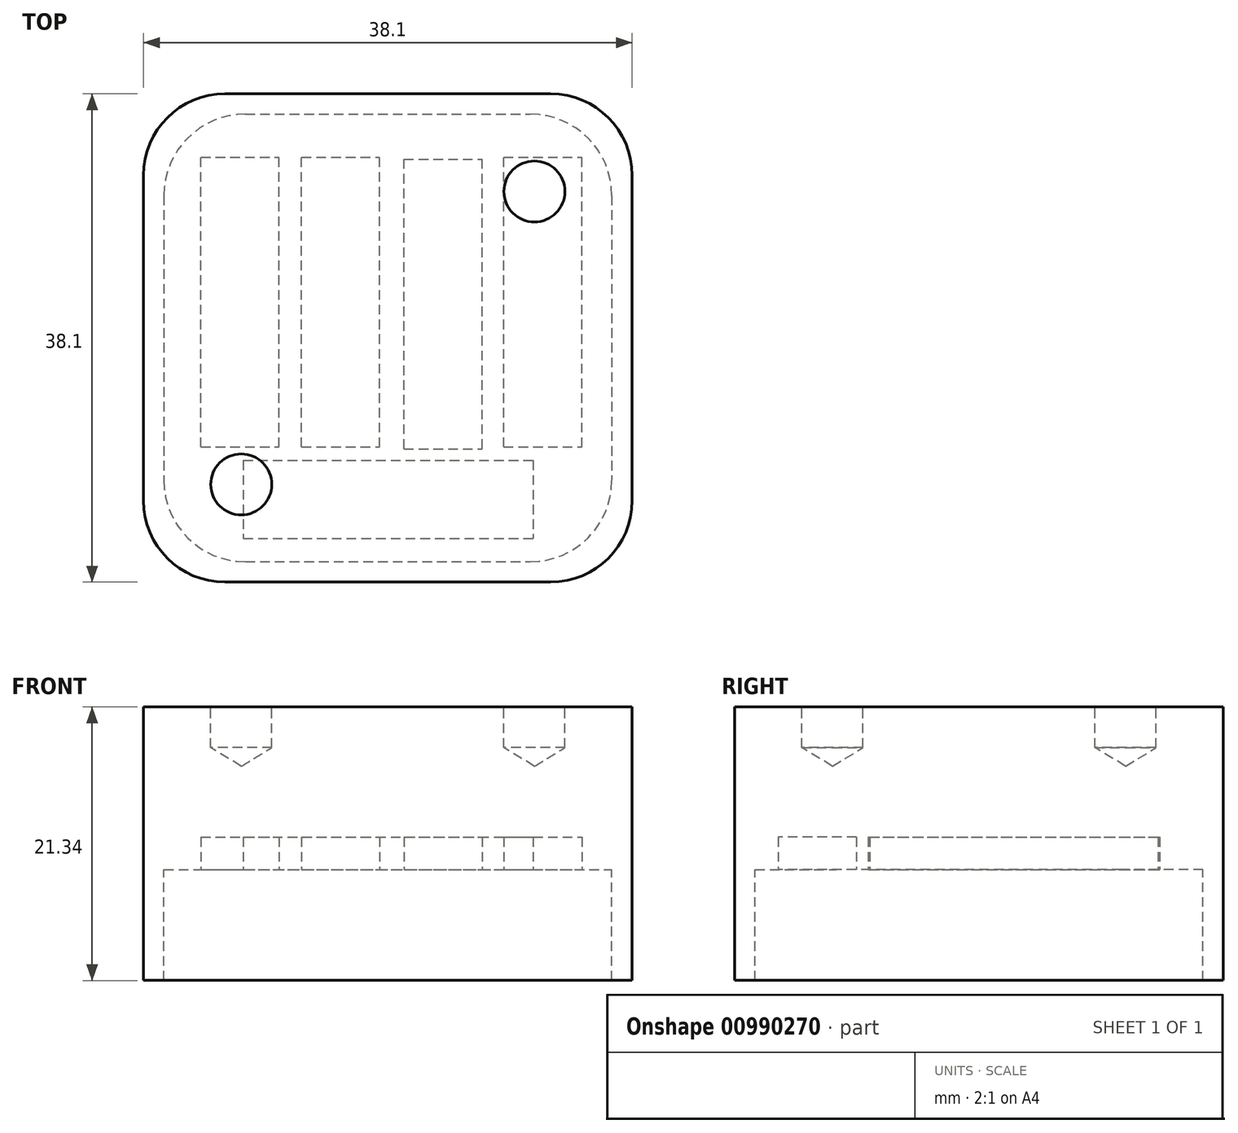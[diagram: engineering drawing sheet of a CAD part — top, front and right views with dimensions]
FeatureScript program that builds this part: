
annotation { "Feature Type Name" : "Feature", "Feature Type Description" : "" }
export const myFeature = defineFeature(function(context is Context, id is Id, definition is map)
    precondition{}
    {
        {
            var Q0;
            Q0=qCreatedBy(makeId("Top.planeOp"),FACE);
            var sketch = newSketch(context, id + "F0", { "sketchPlane" : qUnion([Q0])});
            skLineSegment(sketch, "E0.bottom", {"start": v(15.01, 15.04) * mm, "end": v(40.41, 15.04) * mm});
            skLineSegment(sketch, "E0.top", {"start": v(15.01, -23.06) * mm, "end": v(40.41, -23.06) * mm});
            skLineSegment(sketch, "E0.left", {"start": v(8.66, 8.7) * mm, "end": v(8.66, -16.7) * mm});
            skLineSegment(sketch, "E0.right", {"start": v(46.76, 8.7) * mm, "end": v(46.76, -16.7) * mm});
            skPoint(sketch, "E1.visualSharp", {"position": v(46.76, 15.04) * mm});
            skArc(sketch, "E1.filletArc", {"start": v(46.76, 8.7) * mm, "mid": v(44.9, 13.19) * mm, "end": v(40.41, 15.04) * mm});
            skPoint(sketch, "E2.visualSharp", {"position": v(8.66, 15.04) * mm});
            skArc(sketch, "E2.filletArc", {"start": v(15.01, 15.04) * mm, "mid": v(10.52, 13.19) * mm, "end": v(8.66, 8.7) * mm});
            skPoint(sketch, "E3.visualSharp", {"position": v(8.66, -23.06) * mm});
            skArc(sketch, "E3.filletArc", {"start": v(8.66, -16.7) * mm, "mid": v(10.52, -21.2) * mm, "end": v(15.01, -23.06) * mm});
            skPoint(sketch, "E4.visualSharp", {"position": v(46.76, -23.06) * mm});
            skArc(sketch, "E4.filletArc", {"start": v(40.41, -23.06) * mm, "mid": v(44.9, -21.2) * mm, "end": v(46.76, -16.7) * mm});
            skSolve(sketch);
        }
        {
            var Q0;
            Q0 = qSketchRegion(id + "F0", true);
            extrude(context, id + "F1", {"entities" : qUnion([Q0]), "depth" : 12.7 * mm, "offsetDistance" : 25.4 * mm});
        }
        {
            var Q0;
            Q0=makeQuery(id+"F1.opExtrude","CAP_FACE",FACE,{"disambiguationData":[OSD([sQuery(id+"F0.wireOp",EDGE,"E0.bottom"),sQuery(id+"F0.wireOp",EDGE,"E0.top"),sQuery(id+"F0.wireOp",EDGE,"E0.left"),sQuery(id+"F0.wireOp",EDGE,"E0.right"),sQuery(id+"F0.wireOp",EDGE,"E1.filletArc"),sQuery(id+"F0.wireOp",EDGE,"E2.filletArc"),sQuery(id+"F0.wireOp",EDGE,"E3.filletArc"),sQuery(id+"F0.wireOp",EDGE,"E4.filletArc")])],"isStart":false});
            var sketch = newSketch(context, id + "F2", { "sketchPlane" : qUnion([Q0])});
            skLineSegment(sketch, "E5.0", {"start": v(16.6, 13.46) * mm, "end": v(38.82, 13.46) * mm});
            skLineSegment(sketch, "E5.1", {"start": v(10.25, 7.1) * mm, "end": v(10.25, -15.12) * mm});
            skLineSegment(sketch, "E5.2", {"start": v(16.6, -21.47) * mm, "end": v(38.82, -21.47) * mm});
            skLineSegment(sketch, "E5.3", {"start": v(45.17, 7.1) * mm, "end": v(45.17, -15.12) * mm});
            skPoint(sketch, "E6.visualSharp", {"position": v(10.25, -21.47) * mm});
            skArc(sketch, "E6.filletArc", {"start": v(10.25, -15.12) * mm, "mid": v(12.1, -19.6) * mm, "end": v(16.6, -21.47) * mm});
            skPoint(sketch, "E7.visualSharp", {"position": v(45.17, -21.47) * mm});
            skArc(sketch, "E7.filletArc", {"start": v(38.82, -21.47) * mm, "mid": v(43.31, -19.6) * mm, "end": v(45.17, -15.12) * mm});
            skPoint(sketch, "E8.visualSharp", {"position": v(45.17, 13.46) * mm});
            skArc(sketch, "E8.filletArc", {"start": v(45.17, 7.1) * mm, "mid": v(43.31, 11.6) * mm, "end": v(38.82, 13.46) * mm});
            skPoint(sketch, "E9.visualSharp", {"position": v(10.25, 13.46) * mm});
            skArc(sketch, "E9.filletArc", {"start": v(16.6, 13.46) * mm, "mid": v(12.1, 11.6) * mm, "end": v(10.25, 7.1) * mm});
            skSolve(sketch);
        }
        {
            var Q0;
            Q0=makeQuery(id+"F2.imprint","IMPRINT",FACE,{"disambiguationData":[TD([[makeQuery(id+"F2.imprint","IMPRINT",EDGE,{"derivedFrom":sQuery(id+"F2.wireOp",EDGE,"E5.0")}),1.0]])]});
            extrude(context, id + "F3", {"entities" : qUnion([Q0]), "operationType" : NewBodyOperationType.ADD, "oppositeDirection" : true, "depth" : 21.34 * mm, "offsetDistance" : 25.4 * mm});
        }
        {
            var Q0;
            Q0=makeQuery(id+"F1.opExtrude","CAP_FACE",FACE,{"disambiguationData":[OSD([sQuery(id+"F0.wireOp",EDGE,"E0.bottom"),sQuery(id+"F0.wireOp",EDGE,"E0.top"),sQuery(id+"F0.wireOp",EDGE,"E0.left"),sQuery(id+"F0.wireOp",EDGE,"E0.right"),sQuery(id+"F0.wireOp",EDGE,"E1.filletArc"),sQuery(id+"F0.wireOp",EDGE,"E2.filletArc"),sQuery(id+"F0.wireOp",EDGE,"E3.filletArc"),sQuery(id+"F0.wireOp",EDGE,"E4.filletArc")])],"isStart":false});
            var sketch = newSketch(context, id + "F4", { "sketchPlane" : qUnion([Q0])});
            skSolve(sketch);
        }
        {
            var Q0;
            Q0=makeQuery(id+"F4.imprint","IMPRINT",FACE,{"disambiguationData":[TD([[makeQuery(id+"F4.imprint","IMPRINT",EDGE,{"derivedFrom":makeQuery(id+"F1.opExtrude","CAP_EDGE",EDGE,{"disambiguationData":[OSD([sQuery(id+"F0.wireOp",EDGE,"E0.bottom")])],"isStart":false})}),-1.0]])]});
            var sketch = newSketch(context, id + "F5", { "sketchPlane" : qUnion([Q0])});
            skPoint(sketch, "E10", {"position": v(16.28, -15.44) * mm});
            skPoint(sketch, "E11", {"position": v(39.14, 7.42) * mm});
            skSolve(sketch);
        }
        {
            var Q0;
            Q0=sQuery(id+"F5.wireOp",VERTEX,"E10");
            var Q1;
            Q1=sQuery(id+"F5.wireOp",VERTEX,"E11");
            var Q2;
            Q2=makeQuery(id+"F1.opExtrude","SWEPT_BODY",BODY,{"disambiguationData":[OSD([sQuery(id+"F0.wireOp",EDGE,"E0.bottom"),sQuery(id+"F0.wireOp",EDGE,"E0.top"),sQuery(id+"F0.wireOp",EDGE,"E0.left"),sQuery(id+"F0.wireOp",EDGE,"E0.right"),sQuery(id+"F0.wireOp",EDGE,"E1.filletArc"),sQuery(id+"F0.wireOp",EDGE,"E2.filletArc"),sQuery(id+"F0.wireOp",EDGE,"E3.filletArc"),sQuery(id+"F0.wireOp",EDGE,"E4.filletArc")])]});
            hole(context, id + "F6", {"style" : HoleStyle.SIMPLE, "endStyle" : HoleEndStyle.BLIND, "holeDiameter" : 4.76 * mm, "majorDiameter" : 6.35 * mm, "holeDepth" : 3.17 * mm, "isTappedThrough" : true, "tappedDepth" : 12.7 * mm, "tapClearance" : 3, "locations" : qUnion([Q0, Q1]), "scope" : qUnion([Q2])});
        }
        {
            var Q0;
            Q0=makeQuery(id+"F1.opExtrude","CAP_FACE",FACE,{"disambiguationData":[OSD([sQuery(id+"F0.wireOp",EDGE,"E0.bottom"),sQuery(id+"F0.wireOp",EDGE,"E0.top"),sQuery(id+"F0.wireOp",EDGE,"E0.left"),sQuery(id+"F0.wireOp",EDGE,"E0.right"),sQuery(id+"F0.wireOp",EDGE,"E1.filletArc"),sQuery(id+"F0.wireOp",EDGE,"E2.filletArc"),sQuery(id+"F0.wireOp",EDGE,"E3.filletArc"),sQuery(id+"F0.wireOp",EDGE,"E4.filletArc")])],"isStart":true});
            var sketch = newSketch(context, id + "F7", { "sketchPlane" : qUnion([Q0])});
            skLineSegment(sketch, "E12.bottom", {"start": v(13.13, 12.52) * mm, "end": v(19.23, 12.52) * mm});
            skLineSegment(sketch, "E12.top", {"start": v(13.13, -10.09) * mm, "end": v(19.23, -10.09) * mm});
            skLineSegment(sketch, "E12.left", {"start": v(13.13, 12.52) * mm, "end": v(13.13, -10.09) * mm});
            skLineSegment(sketch, "E12.right", {"start": v(19.23, 12.52) * mm, "end": v(19.23, -10.09) * mm});
            skLineSegment(sketch, "E13.bottom", {"start": v(20.99, 12.52) * mm, "end": v(27.08, 12.52) * mm});
            skLineSegment(sketch, "E13.top", {"start": v(20.99, -10.09) * mm, "end": v(27.08, -10.09) * mm});
            skLineSegment(sketch, "E13.left", {"start": v(20.99, 12.52) * mm, "end": v(20.99, -10.09) * mm});
            skLineSegment(sketch, "E13.right", {"start": v(27.08, 12.52) * mm, "end": v(27.08, -10.09) * mm});
            skLineSegment(sketch, "E14.bottom", {"start": v(28.97, 12.66) * mm, "end": v(35.06, 12.66) * mm});
            skLineSegment(sketch, "E14.top", {"start": v(28.97, -9.95) * mm, "end": v(35.06, -9.95) * mm});
            skLineSegment(sketch, "E14.left", {"start": v(28.97, 12.66) * mm, "end": v(28.97, -9.95) * mm});
            skLineSegment(sketch, "E14.right", {"start": v(35.06, 12.66) * mm, "end": v(35.06, -9.95) * mm});
            skLineSegment(sketch, "E15.bottom", {"start": v(36.75, 12.52) * mm, "end": v(42.84, 12.52) * mm});
            skLineSegment(sketch, "E15.top", {"start": v(36.75, -10.09) * mm, "end": v(42.84, -10.09) * mm});
            skLineSegment(sketch, "E15.left", {"start": v(36.75, 12.52) * mm, "end": v(36.75, -10.09) * mm});
            skLineSegment(sketch, "E15.right", {"start": v(42.84, 12.52) * mm, "end": v(42.84, -10.09) * mm});
            skLineSegment(sketch, "E16.bottom", {"start": v(16.44, 13.56) * mm, "end": v(16.44, 19.66) * mm});
            skLineSegment(sketch, "E16.top", {"start": v(39.05, 13.56) * mm, "end": v(39.05, 19.66) * mm});
            skLineSegment(sketch, "E16.left", {"start": v(16.44, 13.56) * mm, "end": v(39.05, 13.56) * mm});
            skLineSegment(sketch, "E16.right", {"start": v(16.44, 19.66) * mm, "end": v(39.05, 19.66) * mm});
            skSolve(sketch);
        }
        {
            var Q0;
            Q0=makeQuery(id+"F7.imprint","IMPRINT",FACE,{"disambiguationData":[TD([[makeQuery(id+"F7.imprint","IMPRINT",EDGE,{"derivedFrom":sQuery(id+"F7.wireOp",EDGE,"E12.bottom")}),-1.0]])]});
            var Q1;
            Q1=makeQuery(id+"F7.imprint","IMPRINT",FACE,{"disambiguationData":[TD([[makeQuery(id+"F7.imprint","IMPRINT",EDGE,{"derivedFrom":sQuery(id+"F7.wireOp",EDGE,"E16.bottom")}),-1.0]])]});
            var Q2;
            Q2=makeQuery(id+"F7.imprint","IMPRINT",FACE,{"disambiguationData":[TD([[makeQuery(id+"F7.imprint","IMPRINT",EDGE,{"derivedFrom":sQuery(id+"F7.wireOp",EDGE,"E13.bottom")}),-1.0]])]});
            var Q3;
            Q3=makeQuery(id+"F7.imprint","IMPRINT",FACE,{"disambiguationData":[TD([[makeQuery(id+"F7.imprint","IMPRINT",EDGE,{"derivedFrom":sQuery(id+"F7.wireOp",EDGE,"E14.bottom")}),-1.0]])]});
            var Q4;
            Q4=makeQuery(id+"F7.imprint","IMPRINT",FACE,{"disambiguationData":[TD([[makeQuery(id+"F7.imprint","IMPRINT",EDGE,{"derivedFrom":sQuery(id+"F7.wireOp",EDGE,"E15.bottom")}),-1.0]])]});
            extrude(context, id + "F8", {"entities" : qUnion([Q0, Q1, Q2, Q3, Q4]), "operationType" : NewBodyOperationType.REMOVE, "depth" : 2.54 * mm, "offsetDistance" : 25.4 * mm});
        }
        {
            var Q0;
            Q0=makeQuery(id+"F7.imprint","IMPRINT",FACE,{"disambiguationData":[TD([[makeQuery(id+"F7.imprint","IMPRINT",EDGE,{"derivedFrom":sQuery(id+"F7.wireOp",EDGE,"E16.bottom")}),-1.0]])]});
            var Q1;
            Q1=makeQuery(id+"F7.imprint","IMPRINT",FACE,{"disambiguationData":[TD([[makeQuery(id+"F7.imprint","IMPRINT",EDGE,{"derivedFrom":sQuery(id+"F7.wireOp",EDGE,"E12.bottom")}),-1.0]])]});
            var Q2;
            Q2=makeQuery(id+"F7.imprint","IMPRINT",FACE,{"disambiguationData":[TD([[makeQuery(id+"F7.imprint","IMPRINT",EDGE,{"derivedFrom":sQuery(id+"F7.wireOp",EDGE,"E13.bottom")}),-1.0]])]});
            var Q3;
            Q3=makeQuery(id+"F7.imprint","IMPRINT",FACE,{"disambiguationData":[TD([[makeQuery(id+"F7.imprint","IMPRINT",EDGE,{"derivedFrom":sQuery(id+"F7.wireOp",EDGE,"E14.bottom")}),-1.0]])]});
            var Q4;
            Q4=makeQuery(id+"F7.imprint","IMPRINT",FACE,{"disambiguationData":[TD([[makeQuery(id+"F7.imprint","IMPRINT",EDGE,{"derivedFrom":sQuery(id+"F7.wireOp",EDGE,"E15.bottom")}),-1.0]])]});
            extrude(context, id + "F9", {"entities" : qUnion([Q0, Q1, Q2, Q3, Q4]), "operationType" : NewBodyOperationType.REMOVE, "oppositeDirection" : true, "depth" : 2.54 * mm, "offsetDistance" : 25.4 * mm});
        }
    });
